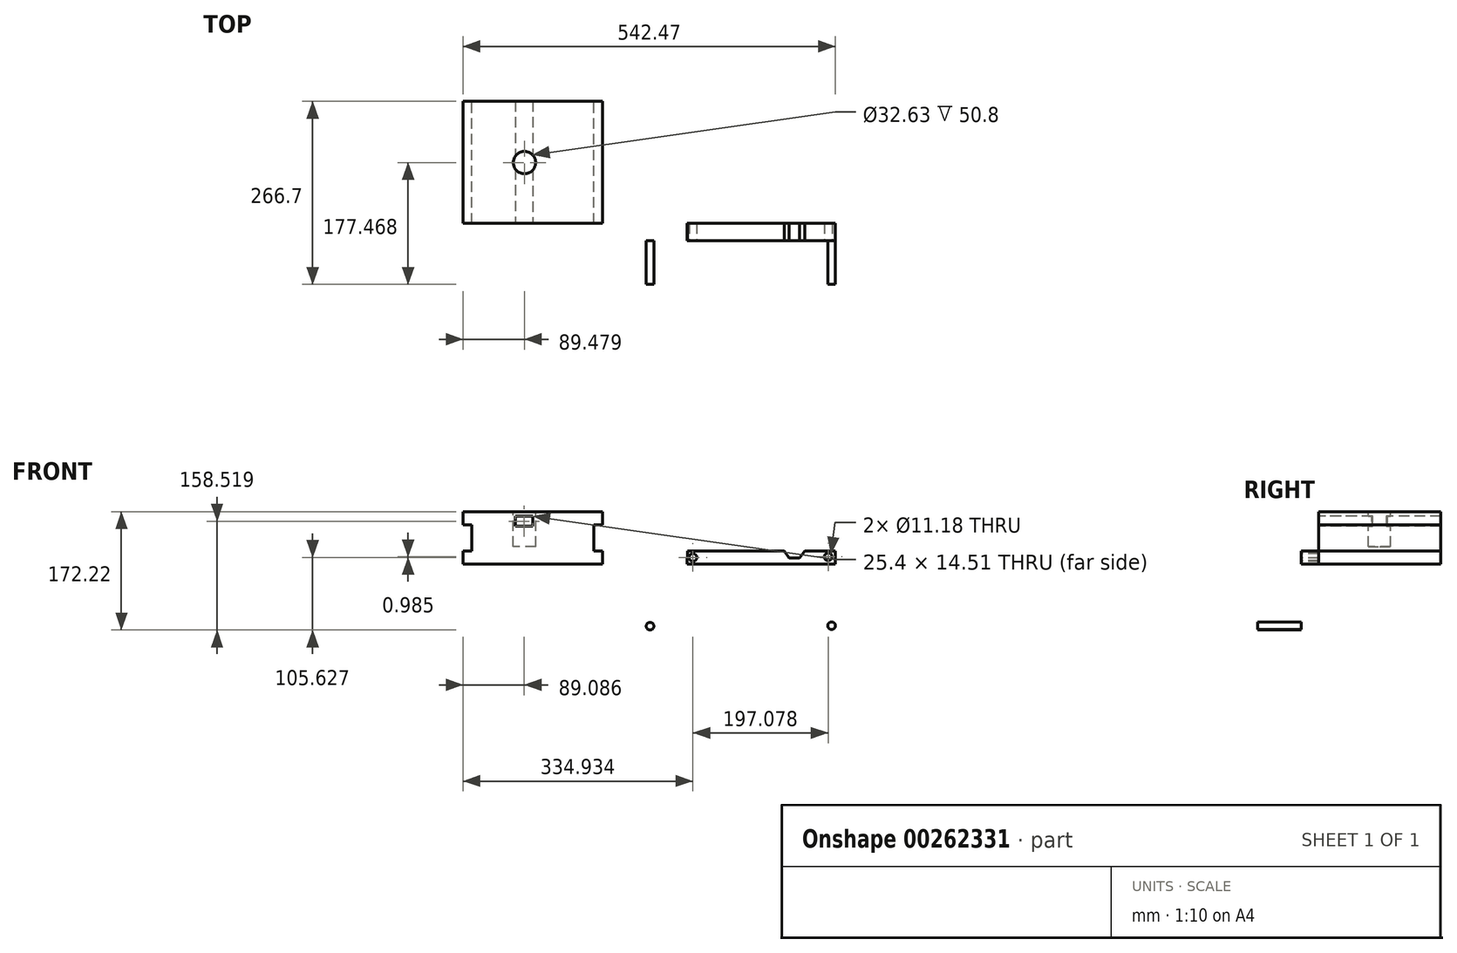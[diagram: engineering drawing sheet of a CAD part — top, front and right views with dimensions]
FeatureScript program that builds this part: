
annotation { "Feature Type Name" : "Feature", "Feature Type Description" : "" }
export const myFeature = defineFeature(function(context is Context, id is Id, definition is map)
    precondition{}
    {
        {
            var Q0;
            Q0=qCreatedBy(makeId("Front.planeOp"),FACE);
            var sketch = newSketch(context, id + "F0", { "sketchPlane" : qUnion([Q0])});
            skLineSegment(sketch, "E0", {"start": v(-71.55, 0) * mm, "end": v(131.65, 0) * mm});
            skLineSegment(sketch, "E1", {"start": v(131.65, 0) * mm, "end": v(131.65, 19.05) * mm});
            skLineSegment(sketch, "E2", {"start": v(131.65, 19.05) * mm, "end": v(-58.85, 19.05) * mm});
            skLineSegment(sketch, "E3", {"start": v(-71.55, 19.05) * mm, "end": v(-71.55, 0) * mm});
            skLineSegment(sketch, "E4", {"start": v(-71.55, 19.05) * mm, "end": v(-58.85, 19.05) * mm});
            skLineSegment(sketch, "E5", {"start": v(131.65, 19.05) * mm, "end": v(118.95, 19.05) * mm});
            skLineSegment(sketch, "E6", {"start": v(118.95, 19.05) * mm, "end": v(118.95, 57.15) * mm});
            skLineSegment(sketch, "E7", {"start": v(118.95, 57.15) * mm, "end": v(131.65, 57.15) * mm});
            skLineSegment(sketch, "E8", {"start": v(131.65, 57.15) * mm, "end": v(131.65, 76.2) * mm});
            skPoint(sketch, "E9.end.orphan", {"position": v(-71.55, 80.4) * mm});
            skPoint(sketch, "E10.end.orphan", {"position": v(-71.55, 76.16) * mm});
            skLineSegment(sketch, "E11", {"start": v(131.65, 76.2) * mm, "end": v(-71.55, 76.16) * mm});
            skLineSegment(sketch, "E12", {"start": v(-58.85, 19.05) * mm, "end": v(-58.85, 57.15) * mm});
            skLineSegment(sketch, "E13", {"start": v(-58.85, 57.15) * mm, "end": v(-71.55, 57.15) * mm});
            skLineSegment(sketch, "E14", {"start": v(-71.55, 57.15) * mm, "end": v(-71.55, 76.2) * mm});
            skLineSegment(sketch, "E15", {"start": v(-58.85, 57.15) * mm, "end": v(17.35, 57.15) * mm});
            skLineSegment(sketch, "E16", {"start": v(118.95, 57.15) * mm, "end": v(42.75, 57.15) * mm});
            skLineSegment(sketch, "E17", {"start": v(17.35, 57.15) * mm, "end": v(17.35, 38.1) * mm});
            skLineSegment(sketch, "E18", {"start": v(42.75, 57.15) * mm, "end": v(42.75, 38.1) * mm});
            skLineSegment(sketch, "E19", {"start": v(42.75, 38.1) * mm, "end": v(17.35, 38.1) * mm});
            skLineSegment(sketch, "E20", {"start": v(17.35, 57.15) * mm, "end": v(42.75, 57.15) * mm});
            skSolve(sketch);
        }
        {
            var Q0;
            Q0=makeQuery(id+"F0.imprint","IMPRINT",FACE,{"disambiguationData":[TD([[makeQuery(id+"F0.imprint","IMPRINT",EDGE,{"derivedFrom":sQuery(id+"F0.wireOp",EDGE,"E2")}),-1.0]])]});
            var Q1;
            Q1=makeQuery(id+"F0.imprint","IMPRINT",FACE,{"disambiguationData":[TD([[makeQuery(id+"F0.imprint","IMPRINT",EDGE,{"derivedFrom":sQuery(id+"F0.wireOp",EDGE,"E0")}),1.0]])]});
            var Q2;
            Q2=makeQuery(id+"F0.imprint","IMPRINT",FACE,{"disambiguationData":[TD([[makeQuery(id+"F0.imprint","IMPRINT",EDGE,{"derivedFrom":sQuery(id+"F0.wireOp",EDGE,"E7")}),1.0]])]});
            var Q3;
            Q3=makeQuery(id+"F0.imprint","IMPRINT",FACE,{"disambiguationData":[TD([[makeQuery(id+"F0.imprint","IMPRINT",EDGE,{"derivedFrom":sQuery(id+"F0.wireOp",EDGE,"E17")}),1.0]])]});
            extrude(context, id + "F1", {"entities" : qUnion([Q0, Q1, Q2, Q3]), "depth" : 177.8 * mm});
        }
        {
            var Q0;
            Q0=makeQuery(id+"F1.opExtrude","CAP_FACE",FACE,{"disambiguationData":[OSD([sQuery(id+"F0.wireOp",EDGE,"E0"),sQuery(id+"F0.wireOp",EDGE,"E1"),sQuery(id+"F0.wireOp",EDGE,"E3"),sQuery(id+"F0.wireOp",EDGE,"E4"),sQuery(id+"F0.wireOp",EDGE,"E5"),sQuery(id+"F0.wireOp",EDGE,"E6"),sQuery(id+"F0.wireOp",EDGE,"E7"),sQuery(id+"F0.wireOp",EDGE,"E8"),sQuery(id+"F0.wireOp",EDGE,"E11"),sQuery(id+"F0.wireOp",EDGE,"E12"),sQuery(id+"F0.wireOp",EDGE,"E13"),sQuery(id+"F0.wireOp",EDGE,"E14")])],"isStart":false});
            var sketch = newSketch(context, id + "F2", { "sketchPlane" : qUnion([Q0])});
            skLineSegment(sketch, "E21", {"start": v(4.84, 69.75) * mm, "end": v(4.84, 55.24) * mm});
            skLineSegment(sketch, "E22", {"start": v(4.84, 55.24) * mm, "end": v(30.24, 55.24) * mm});
            skLineSegment(sketch, "E23", {"start": v(4.84, 69.75) * mm, "end": v(29.98, 69.75) * mm});
            skLineSegment(sketch, "E24", {"start": v(29.98, 69.75) * mm, "end": v(30.24, 55.24) * mm});
            skSolve(sketch);
        }
        {
            var Q0;
            Q0=makeQuery(id+"F2.imprint","IMPRINT",FACE,{"disambiguationData":[TD([[makeQuery(id+"F2.imprint","IMPRINT",EDGE,{"derivedFrom":sQuery(id+"F2.wireOp",EDGE,"E21")}),1.0]])]});
            extrude(context, id + "F3", {"entities" : qUnion([Q0]), "operationType" : NewBodyOperationType.REMOVE, "oppositeDirection" : true, "depth" : 177.8 * mm});
        }
        {
            var Q0;
            Q0=makeQuery(id+"F1.opExtrude","SWEPT_FACE",FACE,{"disambiguationData":[OSD([sQuery(id+"F0.wireOp",EDGE,"E11")])]});
            var sketch = newSketch(context, id + "F4", { "sketchPlane" : qUnion([Q0])});
            skCircle(sketch, "E25", {"center": v(17.94, -89.23) * mm, "radius": 16.31 * mm});
            skSolve(sketch);
        }
        {
            var Q0;
            Q0=makeQuery(id+"F4.imprint","IMPRINT",FACE,{"disambiguationData":[TD([[makeQuery(id+"F4.imprint","IMPRINT",EDGE,{"derivedFrom":sQuery(id+"F4.wireOp",EDGE,"E25")}),1.0]])]});
            extrude(context, id + "F5", {"entities" : qUnion([Q0]), "operationType" : NewBodyOperationType.REMOVE, "oppositeDirection" : true, "depth" : 50.8 * mm});
        }
        {
            var Q0;
            Q0=makeQuery(id+"F1.opExtrude","CAP_FACE",FACE,{"disambiguationData":[OSD([sQuery(id+"F0.wireOp",EDGE,"E0"),sQuery(id+"F0.wireOp",EDGE,"E1"),sQuery(id+"F0.wireOp",EDGE,"E3"),sQuery(id+"F0.wireOp",EDGE,"E4"),sQuery(id+"F0.wireOp",EDGE,"E5"),sQuery(id+"F0.wireOp",EDGE,"E6"),sQuery(id+"F0.wireOp",EDGE,"E7"),sQuery(id+"F0.wireOp",EDGE,"E8"),sQuery(id+"F0.wireOp",EDGE,"E11"),sQuery(id+"F0.wireOp",EDGE,"E12"),sQuery(id+"F0.wireOp",EDGE,"E13"),sQuery(id+"F0.wireOp",EDGE,"E14")])],"isStart":false});
            var sketch = newSketch(context, id + "F6", { "sketchPlane" : qUnion([Q0])});
            skLineSegment(sketch, "E26", {"start": v(255.02, 0) * mm, "end": v(470.92, 0) * mm});
            skLineSegment(sketch, "E27", {"start": v(470.92, 0) * mm, "end": v(470.92, 19.05) * mm});
            skLineSegment(sketch, "E28", {"start": v(470.92, 19.05) * mm, "end": v(255.76, 19.05) * mm});
            skLineSegment(sketch, "E29", {"start": v(255.76, 19.05) * mm, "end": v(255.02, 0) * mm});
            skSolve(sketch);
        }
        {
            var Q0;
            Q0=makeQuery(id+"F6.imprint","IMPRINT",FACE,{"disambiguationData":[TD([[makeQuery(id+"F6.imprint","IMPRINT",EDGE,{"derivedFrom":sQuery(id+"F6.wireOp",EDGE,"E26")}),1.0]])]});
            extrude(context, id + "F7", {"entities" : qUnion([Q0]), "depth" : 25.4 * mm});
        }
        {
            var Q0;
            Q0=makeQuery(id+"F7.opExtrude","CAP_FACE",FACE,{"disambiguationData":[OSD([sQuery(id+"F6.wireOp",EDGE,"E26"),sQuery(id+"F6.wireOp",EDGE,"E27"),sQuery(id+"F6.wireOp",EDGE,"E28"),sQuery(id+"F6.wireOp",EDGE,"E29")])],"isStart":false});
            var sketch = newSketch(context, id + "F8", { "sketchPlane" : qUnion([Q0])});
            skCircle(sketch, "E30", {"center": v(266.3, 9.1) * mm, "radius": 5.59 * mm});
            skCircle(sketch, "E31", {"center": v(460.52, 9.53) * mm, "radius": 5.59 * mm});
            skPoint(sketch, "E31.centerSnap0", {"position": v(470.92, 9.53) * mm});
            skLineSegment(sketch, "E32", {"start": v(396.32, 19.05) * mm, "end": v(403.7, 8.72) * mm});
            skLineSegment(sketch, "E33", {"start": v(403.7, 8.72) * mm, "end": v(418.95, 8.72) * mm});
            skLineSegment(sketch, "E34", {"start": v(418.95, 8.72) * mm, "end": v(426.34, 19.05) * mm});
            skSolve(sketch);
        }
        {
            var Q0;
            {var subQ0=sQuery(id+"F8.wireOp",EDGE,"E32");Q0=makeQuery(id+"F8.imprint","IMPRINT",FACE,{"disambiguationData":[TD([[makeQuery(id+"F8.imprint","IMPRINT",EDGE,{"derivedFrom":subQ0}),1.0]])]});}
            extrude(context, id + "F9", {"entities" : qUnion([Q0]), "operationType" : NewBodyOperationType.REMOVE, "oppositeDirection" : true, "depth" : 25.4 * mm});
        }
        {
            var Q0;
            Q0=makeQuery(id+"F7.opExtrude","CAP_FACE",FACE,{"disambiguationData":[OSD([sQuery(id+"F6.wireOp",EDGE,"E26"),sQuery(id+"F6.wireOp",EDGE,"E27"),sQuery(id+"F6.wireOp",EDGE,"E28"),sQuery(id+"F6.wireOp",EDGE,"E29")])],"isStart":false});
            var sketch = newSketch(context, id + "F10", { "sketchPlane" : qUnion([Q0])});
            skCircle(sketch, "E35", {"center": v(263.38, 9.6) * mm, "radius": 5.59 * mm});
            skCircle(sketch, "E36", {"center": v(461.45, 9.6) * mm, "radius": 5.59 * mm});
            skSolve(sketch);
        }
        {
            var Q0;
            Q0=makeQuery(id+"F10.imprint","IMPRINT",FACE,{"disambiguationData":[TD([[makeQuery(id+"F10.imprint","IMPRINT",EDGE,{"derivedFrom":sQuery(id+"F10.wireOp",EDGE,"E35")}),1.0]])]});
            extrude(context, id + "F11", {"entities" : qUnion([Q0]), "operationType" : NewBodyOperationType.REMOVE, "oppositeDirection" : true, "depth" : 25.4 * mm});
        }
        {
            var Q0;
            Q0=makeQuery(id+"F7.opExtrude","CAP_FACE",FACE,{"disambiguationData":[OSD([sQuery(id+"F6.wireOp",EDGE,"E26"),sQuery(id+"F6.wireOp",EDGE,"E27"),sQuery(id+"F6.wireOp",EDGE,"E28"),sQuery(id+"F6.wireOp",EDGE,"E29")])],"isStart":false});
            var sketch = newSketch(context, id + "F12", { "sketchPlane" : qUnion([Q0])});
            skCircle(sketch, "E37", {"center": v(460.46, 10.6) * mm, "radius": 5.59 * mm});
            skSolve(sketch);
        }
        {
            var Q0;
            Q0=makeQuery(id+"F12.imprint","IMPRINT",FACE,{"disambiguationData":[TD([[makeQuery(id+"F12.imprint","IMPRINT",EDGE,{"derivedFrom":sQuery(id+"F12.wireOp",EDGE,"E37")}),1.0]])]});
            extrude(context, id + "F13", {"entities" : qUnion([Q0]), "operationType" : NewBodyOperationType.REMOVE, "oppositeDirection" : true, "depth" : 25.4 * mm});
        }
        {
            var Q0;
            Q0=makeQuery(id+"F7.opExtrude","CAP_FACE",FACE,{"disambiguationData":[OSD([sQuery(id+"F6.wireOp",EDGE,"E26"),sQuery(id+"F6.wireOp",EDGE,"E27"),sQuery(id+"F6.wireOp",EDGE,"E28"),sQuery(id+"F6.wireOp",EDGE,"E29")])],"isStart":false});
            var sketch = newSketch(context, id + "F14", { "sketchPlane" : qUnion([Q0])});
            skCircle(sketch, "E38", {"center": v(200.9, -90.43) * mm, "radius": 5.59 * mm});
            skSolve(sketch);
        }
        {
            var Q0;
            Q0=makeQuery(id+"F14.imprint","IMPRINT",FACE,{"disambiguationData":[TD([[makeQuery(id+"F14.imprint","IMPRINT",EDGE,{"derivedFrom":sQuery(id+"F14.wireOp",EDGE,"E38")}),1.0]])]});
            extrude(context, id + "F15", {"entities" : qUnion([Q0]), "depth" : 63.5 * mm});
        }
        {
            var Q0;
            Q0=makeQuery(id+"F7.opExtrude","CAP_FACE",FACE,{"disambiguationData":[OSD([sQuery(id+"F6.wireOp",EDGE,"E26"),sQuery(id+"F6.wireOp",EDGE,"E27"),sQuery(id+"F6.wireOp",EDGE,"E28"),sQuery(id+"F6.wireOp",EDGE,"E29")])],"isStart":false});
            var sketch = newSketch(context, id + "F16", { "sketchPlane" : qUnion([Q0])});
            skCircle(sketch, "E39", {"center": v(465.34, -89.77) * mm, "radius": 5.59 * mm});
            skSolve(sketch);
        }
        {
            var Q0;
            Q0=makeQuery(id+"F16.imprint","IMPRINT",FACE,{"disambiguationData":[TD([[makeQuery(id+"F16.imprint","IMPRINT",EDGE,{"derivedFrom":sQuery(id+"F16.wireOp",EDGE,"E39")}),1.0]])]});
            extrude(context, id + "F17", {"entities" : qUnion([Q0]), "depth" : 63.5 * mm});
        }
    });
